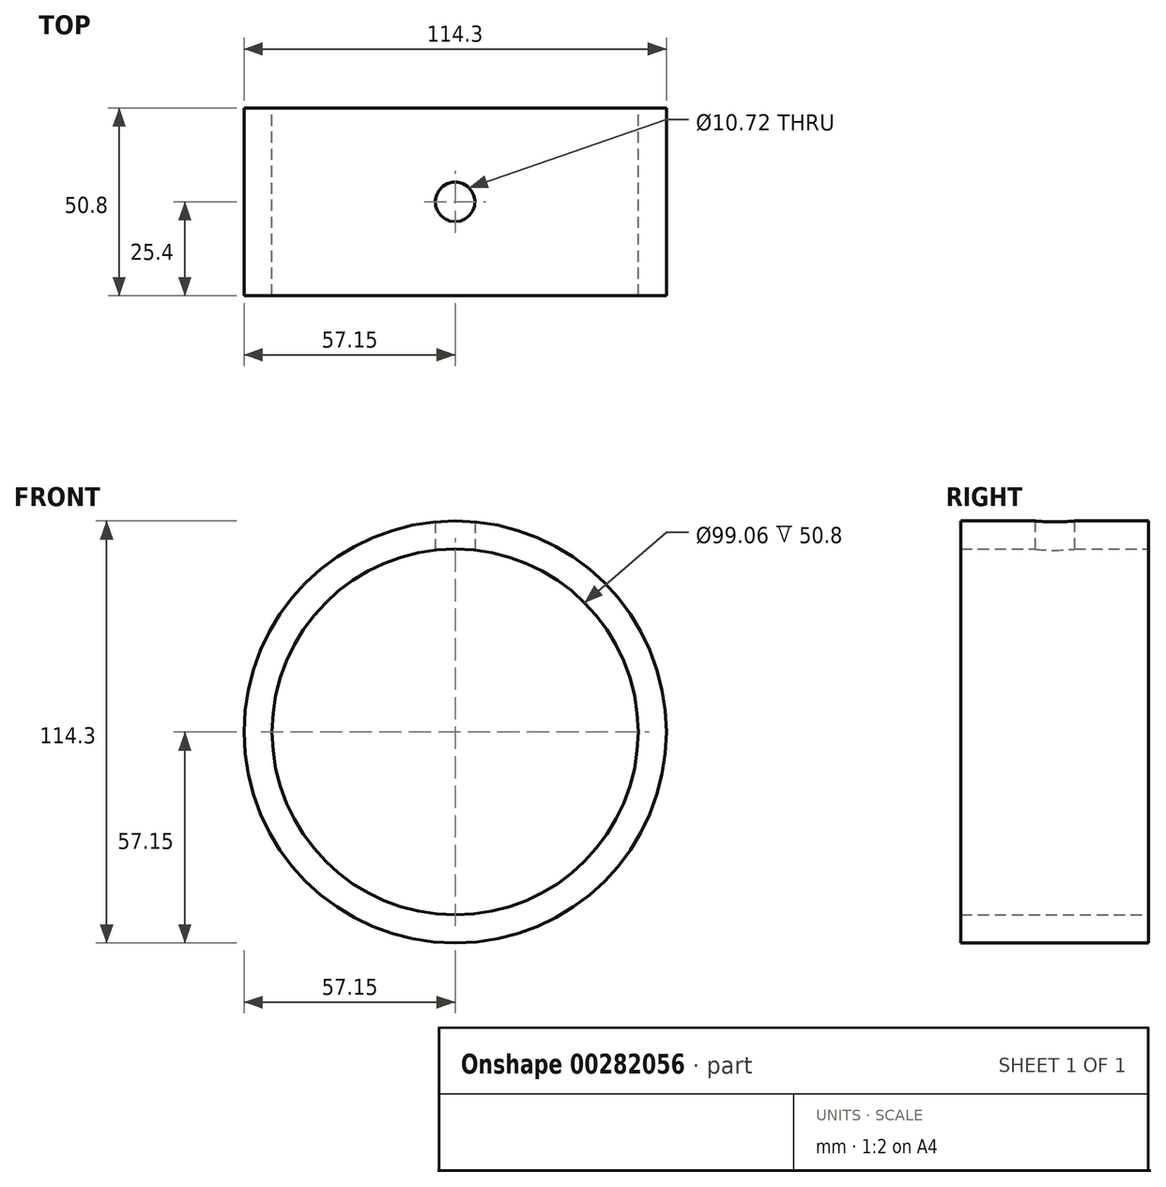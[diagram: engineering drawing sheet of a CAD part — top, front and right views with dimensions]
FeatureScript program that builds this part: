
annotation { "Feature Type Name" : "Feature", "Feature Type Description" : "" }
export const myFeature = defineFeature(function(context is Context, id is Id, definition is map)
    precondition{}
    {
        {
            var Q0;
            Q0=qCreatedBy(makeId("Front.planeOp"),FACE);
            var sketch = newSketch(context, id + "F0", { "sketchPlane" : qUnion([Q0])});
            skCircle(sketch, "E0", {"center": v(0, 0) * mm, "radius": 49.53 * mm});
            skCircle(sketch, "E1", {"center": v(0, 0) * mm, "radius": 57.15 * mm});
            skSolve(sketch);
        }
        {
            var Q0;
            Q0 = qSketchRegion(id + "F0", true);
            extrude(context, id + "F1", {"entities" : qUnion([Q0]), "depth" : 50.8 * mm, "symmetric" : true});
        }
        {
            var Q0;
            Q0=qCreatedBy(makeId("Top.planeOp"),FACE);
            var sketch = newSketch(context, id + "F2", { "sketchPlane" : qUnion([Q0])});
            skPoint(sketch, "E2", {"position": v(0, 0) * mm});
            skSolve(sketch);
        }
        {
            var Q0;
            Q0=sQuery(id+"F2.wireOp",VERTEX,"E2");
            var Q1;
            Q1=makeQuery(id+"F1.opExtrude","SWEPT_BODY",BODY,{"disambiguationData":[OSD([sQuery(id+"F0.wireOp",EDGE,"E0"),sQuery(id+"F0.wireOp",EDGE,"E1")])]});
            hole(context, id + "F3", {"style" : HoleStyle.SIMPLE, "endStyle" : HoleEndStyle.THROUGH, "oppositeDirection" : true, "standardTappedOrClearance" : lookupTablePath({ "standard" : "ANSI", "engagement" : "75%", "pitch" : "13 tpi", "size" : "1/2", "type" : "Tapped" }), "standardBlindInLast" : lookupTablePath({ "standard" : "ANSI", "engagement" : "75%", "pitch" : "13 tpi", "size" : "1/2", "type" : "Tapped" }), "holeDiameter" : 10.72 * mm, "showTappedDepth" : true, "tappedDepth" : 21.59 * mm, "tapClearance" : 3, "startFromSketch" : true, "locations" : qUnion([Q0]), "scope" : qUnion([Q1]), "majorDiameter" : 12.7 * mm});
        }
    });
